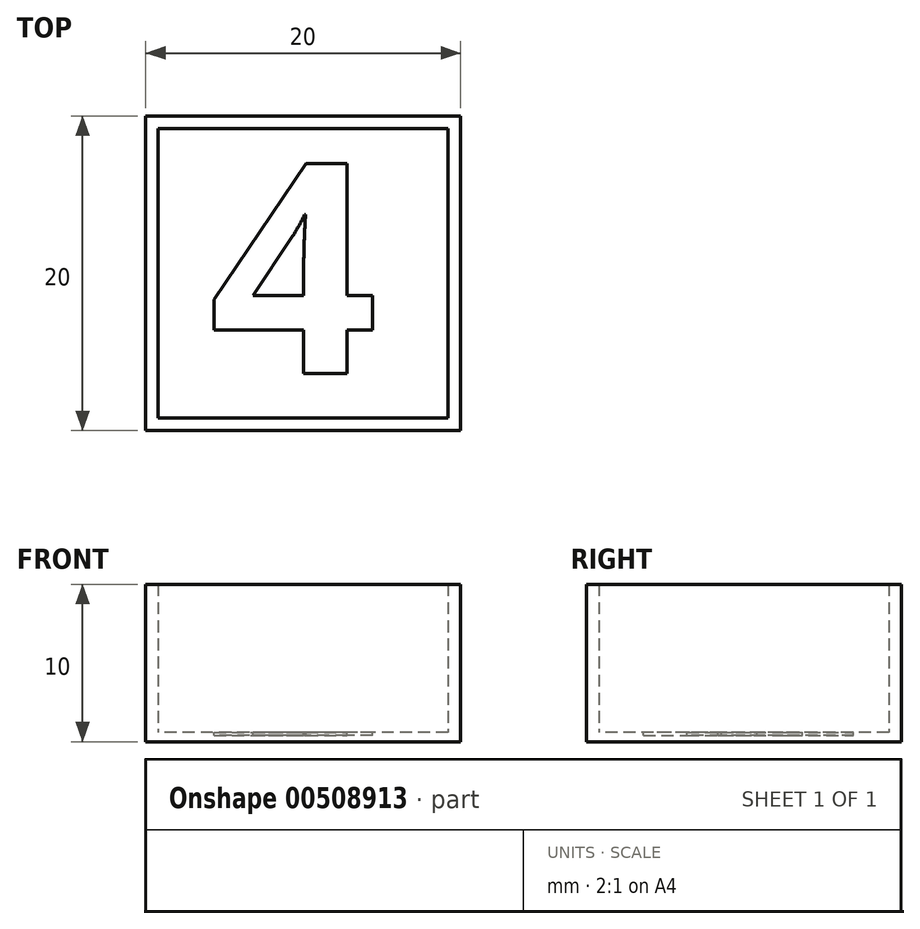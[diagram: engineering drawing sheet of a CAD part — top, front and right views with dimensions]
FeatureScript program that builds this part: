
annotation { "Feature Type Name" : "Feature", "Feature Type Description" : "" }
export const myFeature = defineFeature(function(context is Context, id is Id, definition is map)
    precondition{}
    {
        {
            var Q0;
            Q0=qCreatedBy(makeId("Top.planeOp"),FACE);
            var sketch = newSketch(context, id + "F0", { "sketchPlane" : qUnion([Q0])});
            skLineSegment(sketch, "E0.bottom", {"start": v(10, 10) * mm, "end": v(-10, 10) * mm});
            skLineSegment(sketch, "E0.top", {"start": v(10, -10) * mm, "end": v(-10, -10) * mm});
            skLineSegment(sketch, "E0.left", {"start": v(10, 10) * mm, "end": v(10, -10) * mm});
            skLineSegment(sketch, "E0.right", {"start": v(-10, 10) * mm, "end": v(-10, -10) * mm});
            skPoint(sketch, "E0.middle", {"position": v(0, 0) * mm});
            skLineSegment(sketch, "E1.0", {"start": v(9.2, 9.2) * mm, "end": v(-9.2, 9.2) * mm});
            skLineSegment(sketch, "E1.1", {"start": v(9.2, 9.2) * mm, "end": v(9.2, -9.2) * mm});
            skLineSegment(sketch, "E1.2", {"start": v(9.2, -9.2) * mm, "end": v(-9.2, -9.2) * mm});
            skLineSegment(sketch, "E1.3", {"start": v(-9.2, 9.2) * mm, "end": v(-9.2, -9.2) * mm});
            skSolve(sketch);
        }
        {
            var Q0;
            Q0=makeQuery(id+"F0.imprint","IMPRINT",FACE,{"disambiguationData":[TD([[makeQuery(id+"F0.imprint","IMPRINT",EDGE,{"derivedFrom":sQuery(id+"F0.wireOp",EDGE,"E0.bottom")}),1.0]])]});
            extrude(context, id + "F1", {"entities" : qUnion([Q0]), "depth" : 10 * mm});
        }
        {
            var Q0;
            Q0 = qSketchRegion(id + "F0", true);
            var Q1;
            Q1=makeQuery(id+"F0.imprint","IMPRINT",FACE,{"disambiguationData":[TD([[makeQuery(id+"F0.imprint","IMPRINT",EDGE,{"derivedFrom":sQuery(id+"F0.wireOp",EDGE,"E1.0")}),1.0]])]});
            extrude(context, id + "F2", {"entities" : qUnion([Q0, Q1]), "operationType" : NewBodyOperationType.ADD, "depth" : .6 * mm});
        }
        {
            var Q0;
            Q0=makeQuery(id+"F2.opExtrude","CAP_FACE",FACE,{"disambiguationData":[OSD([sQuery(id+"F0.wireOp",EDGE,"E0.bottom"),sQuery(id+"F0.wireOp",EDGE,"E0.top"),sQuery(id+"F0.wireOp",EDGE,"E0.left"),sQuery(id+"F0.wireOp",EDGE,"E0.right")])],"isStart":false});
            var sketch = newSketch(context, id + "F3", { "sketchPlane" : qUnion([Q0])});
            skText(sketch, "E2", { "text": "4", "fontName": "OpenSans-Bold.ttf"});
            const initialGuessF3  = {"E2": [-0.00597, -0.00638, 1, 0, 0.01345]};
            skSetInitialGuess(sketch, initialGuessF3);
            skSolve(sketch);
        }
        {
            var Q0;
            Q0 = qSketchRegion(id + "F3", true);
            extrude(context, id + "F4", {"entities" : qUnion([Q0]), "operationType" : NewBodyOperationType.REMOVE, "oppositeDirection" : true, "depth" : .2 * mm, "offsetDistance" : 25 * mm});
        }
    });
